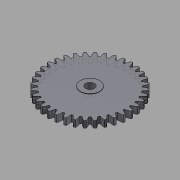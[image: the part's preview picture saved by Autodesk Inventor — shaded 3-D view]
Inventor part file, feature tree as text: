
AUTODESK INVENTOR PART (.ipt)
format: ipt  version: 2015 (Build 190159000, 159)  size: 315,392 bytes
history: native  units: in
note: dims shown in document units (in); Inventor stores cm internally (conversion verified against a paired STEP export)
features: other x13, sketch x4, plane x2
ambient origin geometry x8: Origin, YZ Plane, XZ Plane, XY Plane, X Axis, Y Axis, Z Axis, Center Point
bodies: Solid1 (feature_tree)
feature tree (19):
  other  "Spur Gear2"
  other  "Solid1::Spur Gear2"
  other  "TaggingFeature1"
  sketch  "Sketch1"  dims[d0=0.3937in]
  sketch  "Sketch2"  dims[d16=0.4528in d17=0.0in d41=0.0in d43=0.4528in d46=0.4528in d47=0.0in d48=0.0in]
  sketch  "Sketch3"
  sketch  "Sketch4"
  plane  "XZ Plane_1"
  plane  "Work Plane2"
  other  "Z Axis_1"
  other  "Srf1"
  other  "Srf1::Derived"
  other  "Distance iMate"
  other  "Align iMate"
  other  "Mesh iMate"
  other  "Axis iMate"
  other  "Position iMate"
  other  "Mesh iMate2"
  other  "Start plane iMate"
